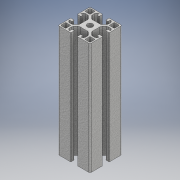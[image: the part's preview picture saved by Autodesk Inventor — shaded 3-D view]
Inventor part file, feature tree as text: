
AUTODESK INVENTOR PART (.ipt)
format: ipt  version: 2018.3 (Build 223284000, 284)  size: 331,264 bytes
history: native  units: mm
features: extrude x1, sketch x1
ambient origin geometry x8: Origin, YZ Plane, XZ Plane, XY Plane, X Axis, Y Axis, Z Axis, Center Point
bodies: Body1 (feature_tree)
feature tree (2):
  extrude  "Extrusión1"  [1 undecoded]
  sketch  "Boceto1"  dims[d0=140.0mm d1=0.0mm]
note: 1 required parameter value undecoded (feature->parameter linkage not recoverable at this tier; creation-order binding heuristic only, values carry confidence <= 0.55)
